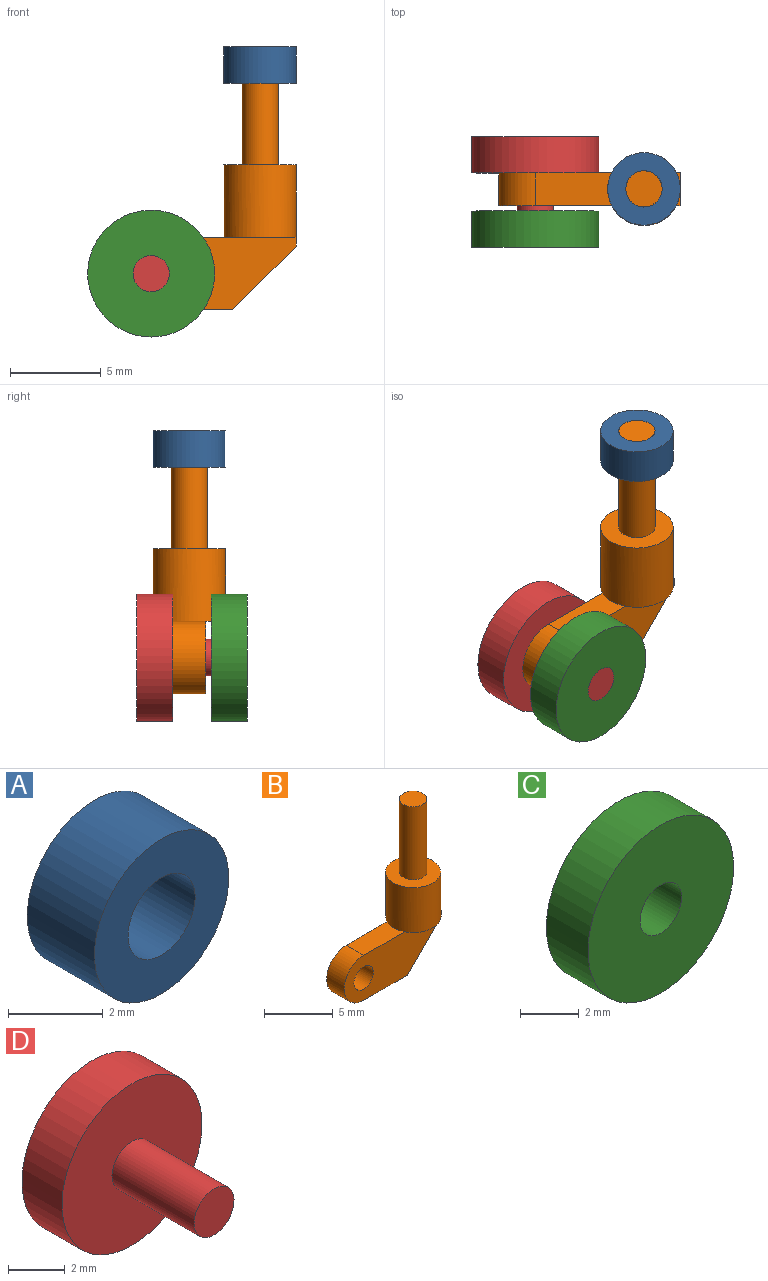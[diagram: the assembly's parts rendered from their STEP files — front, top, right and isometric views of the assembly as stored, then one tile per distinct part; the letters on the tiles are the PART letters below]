
ASSEMBLY  parts=4 mates=4
PART A: 4 faces, bbox 4x2x4 mm
  f0: cylinder r=2mm len=4mm, axis (0,1,0), area 25.1mm2, adj f1,f2
  f1: plane 4x4mm, normal (0,-1,0), area 9.4mm2, adj f0,f3
  f2: plane 4x4mm, normal (0,1,0), area 9.4mm2, adj f0,f3
  f3: cylinder r=1mm len=2mm, axis (0,-1,0), area 12.6mm2, adj f1,f2
PART B: 16 faces, bbox 10x4x14.5 mm
  f0: plane 4.21x1.8mm, normal (0,0,1), area 7.3mm2, adj f6,f7,f9,f15
  f1: plane 0.9x0.21mm, normal (0,0,1), area 0.1mm2, adj f5,f7,f9
  f2: plane 0.9x0.21mm, normal (0,0,1), area 0.1mm2, adj f5,f6,f9
  f3: plane 4.49x1.8mm, normal (0,0,-1), area 8.1mm2, adj f4,f6,f7,f15
  f4: plane 3.51x3.51mm, normal (0.71,0,-0.71), area 8.9mm2, adj f3,f5,f6,f7
  f5: plane 1.8x0.49mm, normal (1,0,0), area 0.9mm2, adj f1,f2,f4,f6,f7
  f6: plane 10x4mm, normal (0,-1,0), area 29mm2, adj f0,f2,f3,f4,f5,f8,f14,f15
  f7: plane 10x4mm, normal (0,1,0), area 29mm2, adj f0,f1,f3,f4,f5,f11,f14,f15
  f8: plane 3.57x1.1mm, normal (0,0,-1), area 2.8mm2, adj f6,f9
  f9: cylinder r=2mm len=4mm, axis (0,0,-1), area 50.3mm2, adj f0,f1,f2,f8,f10,f11
  f10: plane 4x4mm, normal (0,0,1), area 9.4mm2, adj f9,f12
  f11: plane 3.57x1.1mm, normal (0,0,-1), area 2.8mm2, adj f7,f9
  f12: cylinder r=1mm len=6.5mm, axis (0,0,-1), area 40.8mm2, adj f10,f13
  f13: plane 2x2mm, normal (0,0,1), area 3.1mm2, adj f12
  f14: cylinder r=1mm len=2mm, axis (0,-1,0), area 11.3mm2, adj f6,f7
  f15: cylinder r=2mm len=4mm, axis (0,1,0), area 11.3mm2, adj f0,f3,f6,f7
PART C: 4 faces, bbox 7x2x7 mm
  f0: cylinder r=3.5mm len=7mm, axis (0,1,0), area 44mm2, adj f1,f2
  f1: plane 7x7mm, normal (0,-1,0), area 35.3mm2, adj f0,f3
  f2: plane 7x7mm, normal (0,1,0), area 35.3mm2, adj f0,f3
  f3: cylinder r=1mm len=2mm, axis (0,-1,0), area 12.6mm2, adj f1,f2
PART D: 5 faces, bbox 7x6.1x7 mm
  f0: cylinder r=3.5mm len=7mm, axis (0,1,0), area 44mm2, adj f1,f2
  f1: plane 7x7mm, normal (0,-1,0), area 35.3mm2, adj f0,f3
  f2: plane 7x7mm, normal (0,1,0), area 38.5mm2, adj f0
  f3: cylinder r=1mm len=4.1mm, axis (0,1,0), area 25.8mm2, adj f1,f4
  f4: plane 2x2mm, normal (0,-1,0), area 3.1mm2, adj f3
PLACE A rot(axis=(1,0,0),90deg) t=(15.39,-4.79,12.06)mm
PLACE B t=(13.55,-3.89,0.36)mm
PLACE C t=(9.39,-5.99,-0.44)mm
PLACE D t=(9.39,-1.89,-0.44)mm
MATE fastened D.f3 <-> C.f0  axis (0,-1,0) through (9.39,-7.99,-0.44)mm
MATE fastened A.f3 <-> B.f9  axis (0,0,-1) through (15.39,-4.79,12.06)mm
MATE cylindrical D.f3 <-> B.f14  axis (0,1,0) through (9.39,-5.94,-0.44)mm
MATE planar B.f7 <-> D.f0  axis (0,1,0) through (12.17,-3.89,-0.26)mm
